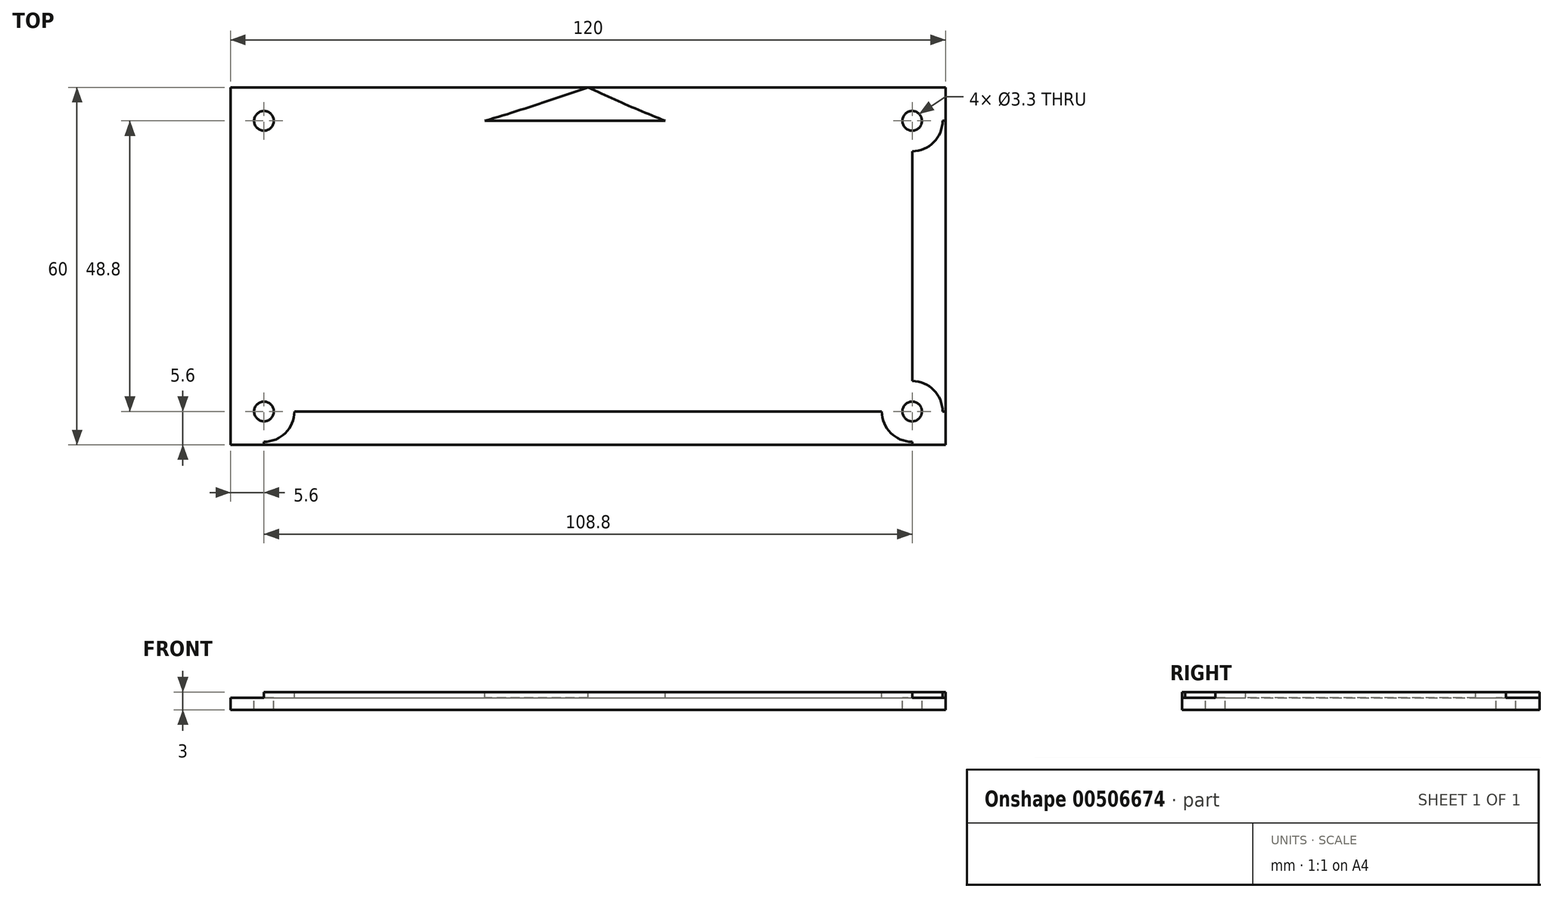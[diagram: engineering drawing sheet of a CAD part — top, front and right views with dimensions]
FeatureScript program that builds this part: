
annotation { "Feature Type Name" : "Feature", "Feature Type Description" : "" }
export const myFeature = defineFeature(function(context is Context, id is Id, definition is map)
    precondition{}
    {
        {
            var Q0;
            Q0=qCreatedBy(makeId("Top.planeOp"),FACE);
            var sketch = newSketch(context, id + "F0", { "sketchPlane" : qUnion([Q0])});
            skLineSegment(sketch, "E0.bottom", {"start": v(4, 0) * mm, "end": v(124, 0) * mm});
            skLineSegment(sketch, "E0.top", {"start": v(4, 60) * mm, "end": v(124, 60) * mm});
            skLineSegment(sketch, "E0.left", {"start": v(4, 0) * mm, "end": v(4, 60) * mm});
            skLineSegment(sketch, "E0.right", {"start": v(124, 0) * mm, "end": v(124, 60) * mm});
            skSolve(sketch);
        }
        {
            var Q0;
            Q0=makeQuery(id+"F0.imprint","IMPRINT",FACE,{"disambiguationData":[TD([[makeQuery(id+"F0.imprint","IMPRINT",EDGE,{"derivedFrom":sQuery(id+"F0.wireOp",EDGE,"E0.bottom")}),1.0]])]});
            extrude(context, id + "F1", {"entities" : qUnion([Q0]), "depth" : 3 * mm});
        }
        {
            var Q0;
            Q0=makeQuery(id+"F1.opExtrude","CAP_FACE",FACE,{"disambiguationData":[OSD([sQuery(id+"F0.wireOp",EDGE,"E0.bottom"),sQuery(id+"F0.wireOp",EDGE,"E0.top"),sQuery(id+"F0.wireOp",EDGE,"E0.left"),sQuery(id+"F0.wireOp",EDGE,"E0.right")])],"isStart":false});
            var sketch = newSketch(context, id + "F2", { "sketchPlane" : qUnion([Q0])});
            skLineSegment(sketch, "E1", {"start": v(9.6, 60) * mm, "end": v(9.6, 0) * mm});
            skLineSegment(sketch, "E2", {"start": v(4, 5.6) * mm, "end": v(124, 5.6) * mm});
            skLineSegment(sketch, "E3", {"start": v(4, 54.4) * mm, "end": v(124, 54.4) * mm});
            skLineSegment(sketch, "E4", {"start": v(118.4, 60) * mm, "end": v(118.4, 0) * mm});
            skCircle(sketch, "E5", {"center": v(9.6, 54.4) * mm, "radius": 5.1 * mm});
            skCircle(sketch, "E6", {"center": v(9.6, 5.6) * mm, "radius": 5.1 * mm});
            skCircle(sketch, "E7", {"center": v(118.4, 5.6) * mm, "radius": 5.1 * mm});
            skCircle(sketch, "E8", {"center": v(118.4, 54.4) * mm, "radius": 5.1 * mm});
            skSolve(sketch);
        }
        {
            var Q0;
            {var subQ0=sQuery(id+"F2.wireOp",EDGE,"E5");var subQ1=sQuery(id+"F2.wireOp",EDGE,"E1");var subQ2=makeQuery(id+"F2.imprint","INTERSECT",VERTEX,{"disambiguationData":[OD(0.0)],"derivedFrom":[subQ1,subQ0]});Q0=makeQuery(id+"F2.imprint","IMPRINT",FACE,{"disambiguationData":[TD([[makeQuery(id+"F2.imprint","IMPRINT",EDGE,{"disambiguationData":[TD([[subQ2,-1.0]])],"derivedFrom":subQ1}),1.0]])]});}
            var Q1;
            {var subQ0=sQuery(id+"F2.wireOp",EDGE,"E3");var subQ1=sQuery(id+"F2.wireOp",EDGE,"E1");var subQ2=makeQuery(id+"F2.imprint","INTERSECT",VERTEX,{"derivedFrom":[subQ1,subQ0]});Q1=makeQuery(id+"F2.imprint","IMPRINT",FACE,{"disambiguationData":[TD([[makeQuery(id+"F2.imprint","IMPRINT",EDGE,{"disambiguationData":[TD([[subQ2,-1.0]])],"derivedFrom":subQ1}),-1.0]])]});}
            var Q2;
            {var subQ0=sQuery(id+"F2.wireOp",EDGE,"E3");var subQ1=sQuery(id+"F2.wireOp",EDGE,"E1");var subQ2=makeQuery(id+"F2.imprint","INTERSECT",VERTEX,{"derivedFrom":[subQ1,subQ0]});Q2=makeQuery(id+"F2.imprint","IMPRINT",FACE,{"disambiguationData":[TD([[makeQuery(id+"F2.imprint","IMPRINT",EDGE,{"disambiguationData":[TD([[subQ2,-1.0]])],"derivedFrom":subQ1}),1.0]])]});}
            var Q3;
            {var subQ0=sQuery(id+"F2.wireOp",EDGE,"E6");var subQ1=sQuery(id+"F2.wireOp",EDGE,"E1");var subQ2=makeQuery(id+"F2.imprint","INTERSECT",VERTEX,{"disambiguationData":[OD(0.0)],"derivedFrom":[subQ1,subQ0]});Q3=makeQuery(id+"F2.imprint","IMPRINT",FACE,{"disambiguationData":[TD([[makeQuery(id+"F2.imprint","IMPRINT",EDGE,{"disambiguationData":[TD([[subQ2,-1.0]])],"derivedFrom":subQ1}),-1.0]])]});}
            var Q4;
            {var subQ0=sQuery(id+"F2.wireOp",EDGE,"E6");var subQ1=sQuery(id+"F2.wireOp",EDGE,"E1");var subQ2=makeQuery(id+"F2.imprint","INTERSECT",VERTEX,{"disambiguationData":[OD(0.0)],"derivedFrom":[subQ1,subQ0]});Q4=makeQuery(id+"F2.imprint","IMPRINT",FACE,{"disambiguationData":[TD([[makeQuery(id+"F2.imprint","IMPRINT",EDGE,{"disambiguationData":[TD([[subQ2,-1.0]])],"derivedFrom":subQ1}),1.0]])]});}
            var Q5;
            {var subQ0=sQuery(id+"F2.wireOp",EDGE,"E2");var subQ1=sQuery(id+"F2.wireOp",EDGE,"E1");var subQ2=makeQuery(id+"F2.imprint","INTERSECT",VERTEX,{"derivedFrom":[subQ1,subQ0]});Q5=makeQuery(id+"F2.imprint","IMPRINT",FACE,{"disambiguationData":[TD([[makeQuery(id+"F2.imprint","IMPRINT",EDGE,{"disambiguationData":[TD([[subQ2,-1.0]])],"derivedFrom":subQ1}),-1.0]])]});}
            var Q6;
            {var subQ0=sQuery(id+"F2.wireOp",EDGE,"E2");var subQ1=sQuery(id+"F2.wireOp",EDGE,"E1");var subQ2=makeQuery(id+"F2.imprint","INTERSECT",VERTEX,{"derivedFrom":[subQ1,subQ0]});Q6=makeQuery(id+"F2.imprint","IMPRINT",FACE,{"disambiguationData":[TD([[makeQuery(id+"F2.imprint","IMPRINT",EDGE,{"disambiguationData":[TD([[subQ2,-1.0]])],"derivedFrom":subQ1}),1.0]])]});}
            var Q7;
            {var subQ0=sQuery(id+"F2.wireOp",EDGE,"E7");var subQ1=sQuery(id+"F2.wireOp",EDGE,"E2");var subQ2=makeQuery(id+"F2.imprint","INTERSECT",VERTEX,{"disambiguationData":[OD(0.0)],"derivedFrom":[subQ1,subQ0]});Q7=makeQuery(id+"F2.imprint","IMPRINT",FACE,{"disambiguationData":[TD([[makeQuery(id+"F2.imprint","IMPRINT",EDGE,{"disambiguationData":[TD([[subQ2,-1.0]])],"derivedFrom":subQ1}),1.0]])]});}
            var Q8;
            {var subQ0=sQuery(id+"F2.wireOp",EDGE,"E7");var subQ1=sQuery(id+"F2.wireOp",EDGE,"E2");var subQ2=makeQuery(id+"F2.imprint","INTERSECT",VERTEX,{"disambiguationData":[OD(0.0)],"derivedFrom":[subQ1,subQ0]});Q8=makeQuery(id+"F2.imprint","IMPRINT",FACE,{"disambiguationData":[TD([[makeQuery(id+"F2.imprint","IMPRINT",EDGE,{"disambiguationData":[TD([[subQ2,-1.0]])],"derivedFrom":subQ1}),-1.0]])]});}
            var Q9;
            {var subQ0=sQuery(id+"F2.wireOp",EDGE,"E4");var subQ1=sQuery(id+"F2.wireOp",EDGE,"E2");var subQ2=makeQuery(id+"F2.imprint","INTERSECT",VERTEX,{"derivedFrom":[subQ1,subQ0]});Q9=makeQuery(id+"F2.imprint","IMPRINT",FACE,{"disambiguationData":[TD([[makeQuery(id+"F2.imprint","IMPRINT",EDGE,{"disambiguationData":[TD([[subQ2,-1.0]])],"derivedFrom":subQ1}),1.0]])]});}
            var Q10;
            {var subQ0=sQuery(id+"F2.wireOp",EDGE,"E4");var subQ1=sQuery(id+"F2.wireOp",EDGE,"E2");var subQ2=makeQuery(id+"F2.imprint","INTERSECT",VERTEX,{"derivedFrom":[subQ1,subQ0]});Q10=makeQuery(id+"F2.imprint","IMPRINT",FACE,{"disambiguationData":[TD([[makeQuery(id+"F2.imprint","IMPRINT",EDGE,{"disambiguationData":[TD([[subQ2,-1.0]])],"derivedFrom":subQ1}),-1.0]])]});}
            var Q11;
            {var subQ0=sQuery(id+"F2.wireOp",EDGE,"E8");var subQ1=sQuery(id+"F2.wireOp",EDGE,"E3");var subQ2=makeQuery(id+"F2.imprint","INTERSECT",VERTEX,{"disambiguationData":[OD(0.0)],"derivedFrom":[subQ1,subQ0]});Q11=makeQuery(id+"F2.imprint","IMPRINT",FACE,{"disambiguationData":[TD([[makeQuery(id+"F2.imprint","IMPRINT",EDGE,{"disambiguationData":[TD([[subQ2,-1.0]])],"derivedFrom":subQ1}),1.0]])]});}
            var Q12;
            {var subQ0=sQuery(id+"F2.wireOp",EDGE,"E8");var subQ1=sQuery(id+"F2.wireOp",EDGE,"E3");var subQ2=makeQuery(id+"F2.imprint","INTERSECT",VERTEX,{"disambiguationData":[OD(0.0)],"derivedFrom":[subQ1,subQ0]});Q12=makeQuery(id+"F2.imprint","IMPRINT",FACE,{"disambiguationData":[TD([[makeQuery(id+"F2.imprint","IMPRINT",EDGE,{"disambiguationData":[TD([[subQ2,-1.0]])],"derivedFrom":subQ1}),-1.0]])]});}
            var Q13;
            {var subQ0=sQuery(id+"F2.wireOp",EDGE,"E4");var subQ1=sQuery(id+"F2.wireOp",EDGE,"E3");var subQ2=makeQuery(id+"F2.imprint","INTERSECT",VERTEX,{"derivedFrom":[subQ1,subQ0]});Q13=makeQuery(id+"F2.imprint","IMPRINT",FACE,{"disambiguationData":[TD([[makeQuery(id+"F2.imprint","IMPRINT",EDGE,{"disambiguationData":[TD([[subQ2,-1.0]])],"derivedFrom":subQ1}),1.0]])]});}
            var Q14;
            {var subQ0=sQuery(id+"F2.wireOp",EDGE,"E4");var subQ1=sQuery(id+"F2.wireOp",EDGE,"E3");var subQ2=makeQuery(id+"F2.imprint","INTERSECT",VERTEX,{"derivedFrom":[subQ1,subQ0]});Q14=makeQuery(id+"F2.imprint","IMPRINT",FACE,{"disambiguationData":[TD([[makeQuery(id+"F2.imprint","IMPRINT",EDGE,{"disambiguationData":[TD([[subQ2,-1.0]])],"derivedFrom":subQ1}),-1.0]])]});}
            var Q15;
            {var subQ0=sQuery(id+"F2.wireOp",EDGE,"E5");var subQ1=sQuery(id+"F2.wireOp",EDGE,"E1");var subQ2=makeQuery(id+"F2.imprint","INTERSECT",VERTEX,{"disambiguationData":[OD(0.0)],"derivedFrom":[subQ1,subQ0]});Q15=makeQuery(id+"F2.imprint","IMPRINT",FACE,{"disambiguationData":[TD([[makeQuery(id+"F2.imprint","IMPRINT",EDGE,{"disambiguationData":[TD([[subQ2,-1.0]])],"derivedFrom":subQ1}),-1.0]])]});}
            var Q16;
            {var subQ1=makeQuery(id+"F1.opExtrude","CAP_EDGE",EDGE,{"disambiguationData":[OSD([sQuery(id+"F0.wireOp",EDGE,"E0.top")])],"isStart":false});var subQ3=sQuery(id+"F2.wireOp",EDGE,"E1");var subQ4=makeQuery(id+"F2.imprint","INTERSECT",VERTEX,{"derivedFrom":[subQ1,subQ3]});Q16=makeQuery(id+"F2.imprint","IMPRINT",FACE,{"disambiguationData":[TD([[makeQuery(id+"F2.imprint","IMPRINT",EDGE,{"disambiguationData":[TD([[subQ4,-1.0]])],"derivedFrom":subQ3}),-1.0]])]});}
            var Q17;
            {var subQ0=makeQuery(id+"F1.opExtrude","CAP_EDGE",EDGE,{"disambiguationData":[OSD([sQuery(id+"F0.wireOp",EDGE,"E0.right")])],"isStart":false});var subQ7=sQuery(id+"F2.wireOp",EDGE,"E3");var subQ8=makeQuery(id+"F2.imprint","INTERSECT",VERTEX,{"derivedFrom":[subQ0,subQ7]});Q17=makeQuery(id+"F2.imprint","IMPRINT",FACE,{"disambiguationData":[TD([[makeQuery(id+"F2.imprint","IMPRINT",EDGE,{"disambiguationData":[TD([[subQ8,1.0]])],"derivedFrom":subQ7}),1.0]])]});}
            var Q18;
            {var subQ0=makeQuery(id+"F1.opExtrude","CAP_EDGE",EDGE,{"disambiguationData":[OSD([sQuery(id+"F0.wireOp",EDGE,"E0.right")])],"isStart":false});var subQ6=sQuery(id+"F2.wireOp",EDGE,"E2");var subQ9=makeQuery(id+"F2.imprint","INTERSECT",VERTEX,{"derivedFrom":[subQ0,subQ6]});Q18=makeQuery(id+"F2.imprint","IMPRINT",FACE,{"disambiguationData":[TD([[makeQuery(id+"F2.imprint","IMPRINT",EDGE,{"disambiguationData":[TD([[subQ9,1.0]])],"derivedFrom":subQ6}),-1.0]])]});}
            var Q19;
            {var subQ1=makeQuery(id+"F1.opExtrude","CAP_EDGE",EDGE,{"disambiguationData":[OSD([sQuery(id+"F0.wireOp",EDGE,"E0.bottom")])],"isStart":false});var subQ3=sQuery(id+"F2.wireOp",EDGE,"E1");var subQ4=makeQuery(id+"F2.imprint","INTERSECT",VERTEX,{"derivedFrom":[subQ1,subQ3]});Q19=makeQuery(id+"F2.imprint","IMPRINT",FACE,{"disambiguationData":[TD([[makeQuery(id+"F2.imprint","IMPRINT",EDGE,{"disambiguationData":[TD([[subQ4,1.0]])],"derivedFrom":subQ3}),-1.0]])]});}
            extrude(context, id + "F3", {"entities" : qUnion([Q0, Q1, Q2, Q3, Q4, Q5, Q6, Q7, Q8, Q9, Q10, Q11, Q12, Q13, Q14, Q15, Q16, Q17, Q18, Q19]), "operationType" : NewBodyOperationType.REMOVE, "oppositeDirection" : true, "depth" : 1 * mm});
        }
        {
            var Q0;
            Q0=makeQuery(id+"F1.opExtrude","CAP_FACE",FACE,{"disambiguationData":[OSD([sQuery(id+"F0.wireOp",EDGE,"E0.bottom"),sQuery(id+"F0.wireOp",EDGE,"E0.top"),sQuery(id+"F0.wireOp",EDGE,"E0.left"),sQuery(id+"F0.wireOp",EDGE,"E0.right")])],"isStart":false});
            var sketch = newSketch(context, id + "F4", { "sketchPlane" : qUnion([Q0])});
            skPoint(sketch, "E9", {"position": v(64, 60) * mm});
            skPoint(sketch, "E10", {"position": v(64, 0) * mm});
            skFitSpline(sketch, "E11", {"points": [v(64, 60) * mm, v(32.93, 51.04) * mm, v(9.74, 49.3) * mm], "startDerivative": vector(-59.28, -19.97) * mm, "endDerivative": vector(-48.96, -1.03) * mm});
            skFitSpline(sketch, "E12", {"points": [v(64, 60) * mm, v(90.16, 50.44) * mm, v(118.4, 49.3) * mm], "startDerivative": vector(51.57, -23.4) * mm, "endDerivative": vector(57.22, 1.98) * mm});
            skFitSpline(sketch, "E13", {"points": [v(64, 0) * mm, v(37.17, 8.05) * mm, v(10.1, 10.68) * mm], "startDerivative": vector(-52.95, 18.65) * mm, "endDerivative": vector(-54.84, 2.72) * mm});
            skFitSpline(sketch, "E14", {"points": [v(64, 0) * mm, v(89.1, 7.6) * mm, v(118.4, 10.7) * mm], "startDerivative": vector(50.43, 17.97) * mm, "endDerivative": vector(58.29, 3.57) * mm});
            skSolve(sketch);
        }
        {
            var Q0;
            Q0 = qSketchRegion(id + "F4", true);
            var Q1;
            {var subQ0=sQuery(id+"F4.wireOp",EDGE,"E11");Q1=makeQuery(id+"F4.imprint","IMPRINT",FACE,{"disambiguationData":[TD([[makeQuery(id+"F4.imprint","IMPRINT",EDGE,{"derivedFrom":subQ0}),-1.0]])]});}
            var Q2;
            {var subQ0=sQuery(id+"F4.wireOp",EDGE,"E12");Q2=makeQuery(id+"F4.imprint","IMPRINT",FACE,{"disambiguationData":[TD([[makeQuery(id+"F4.imprint","IMPRINT",EDGE,{"derivedFrom":subQ0}),1.0]])]});}
            var Q3;
            {var subQ1=makeQuery(id+"F1.opExtrude","CAP_EDGE",EDGE,{"disambiguationData":[OSD([sQuery(id+"F0.wireOp",EDGE,"E0.bottom")])],"isStart":false});var subQ7=sQuery(id+"F2.wireOp",EDGE,"E4");var subQ8=makeQuery(id+"F3.boolean.opBoolean","COPY",EDGE,{"derivedFrom":makeQuery(id+"F3.opExtrude","CAP_EDGE",EDGE,{"disambiguationData":[OSD([subQ7]),TDD([makeQuery(id+"F2.imprint","IMPRINT",EDGE,{"disambiguationData":[TD([[makeQuery(id+"F2.imprint","INTERSECT",VERTEX,{"derivedFrom":[subQ1,subQ7]}),1.0]])],"derivedFrom":subQ7})])],"isStart":true})});Q3=makeQuery(id+"F4.imprint","IMPRINT",FACE,{"disambiguationData":[TD([[makeQuery(id+"F4.imprint","IMPRINT",EDGE,{"derivedFrom":subQ8}),-1.0]])]});}
            var Q4;
            {var subQ0=sQuery(id+"F4.wireOp",EDGE,"E13");Q4=makeQuery(id+"F4.imprint","IMPRINT",FACE,{"disambiguationData":[TD([[makeQuery(id+"F4.imprint","IMPRINT",EDGE,{"derivedFrom":subQ0}),1.0]])]});}
            extrude(context, id + "F5", {"entities" : qUnion([Q0, Q1, Q2, Q3, Q4]), "operationType" : NewBodyOperationType.REMOVE, "oppositeDirection" : true, "depth" : 1 * mm});
        }
        {
            var Q0;
            Q0=sQuery(id+"F2.wireOp",VERTEX,"E5.center");
            var Q1;
            Q1=makeQuery(id+"F1.opExtrude","SWEPT_BODY",BODY,{"disambiguationData":[OSD([sQuery(id+"F0.wireOp",EDGE,"E0.bottom"),sQuery(id+"F0.wireOp",EDGE,"E0.top"),sQuery(id+"F0.wireOp",EDGE,"E0.left"),sQuery(id+"F0.wireOp",EDGE,"E0.right")])]});
            hole(context, id + "F6", {"style" : HoleStyle.SIMPLE, "endStyle" : HoleEndStyle.THROUGH, "holeDiameter" : 3.3 * mm, "tappedDepth" : 12 * mm, "tapClearance" : 3, "locations" : qUnion([Q0]), "scope" : qUnion([Q1])});
        }
        {
            var Q0;
            Q0=sQuery(id+"F2.wireOp",VERTEX,"E8.center");
            var Q1;
            Q1=sQuery(id+"F2.wireOp",VERTEX,"E7.center");
            var Q2;
            Q2=sQuery(id+"F2.wireOp",VERTEX,"E6.center");
            var Q3;
            Q3=makeQuery(id+"F1.opExtrude","SWEPT_BODY",BODY,{"disambiguationData":[OSD([sQuery(id+"F0.wireOp",EDGE,"E0.bottom"),sQuery(id+"F0.wireOp",EDGE,"E0.top"),sQuery(id+"F0.wireOp",EDGE,"E0.left"),sQuery(id+"F0.wireOp",EDGE,"E0.right")])]});
            hole(context, id + "F7", {"style" : HoleStyle.SIMPLE, "endStyle" : HoleEndStyle.THROUGH, "holeDiameter" : 3.3 * mm, "tappedDepth" : 12 * mm, "tapClearance" : 3, "locations" : qUnion([Q0, Q1, Q2]), "scope" : qUnion([Q3])});
        }
    });
